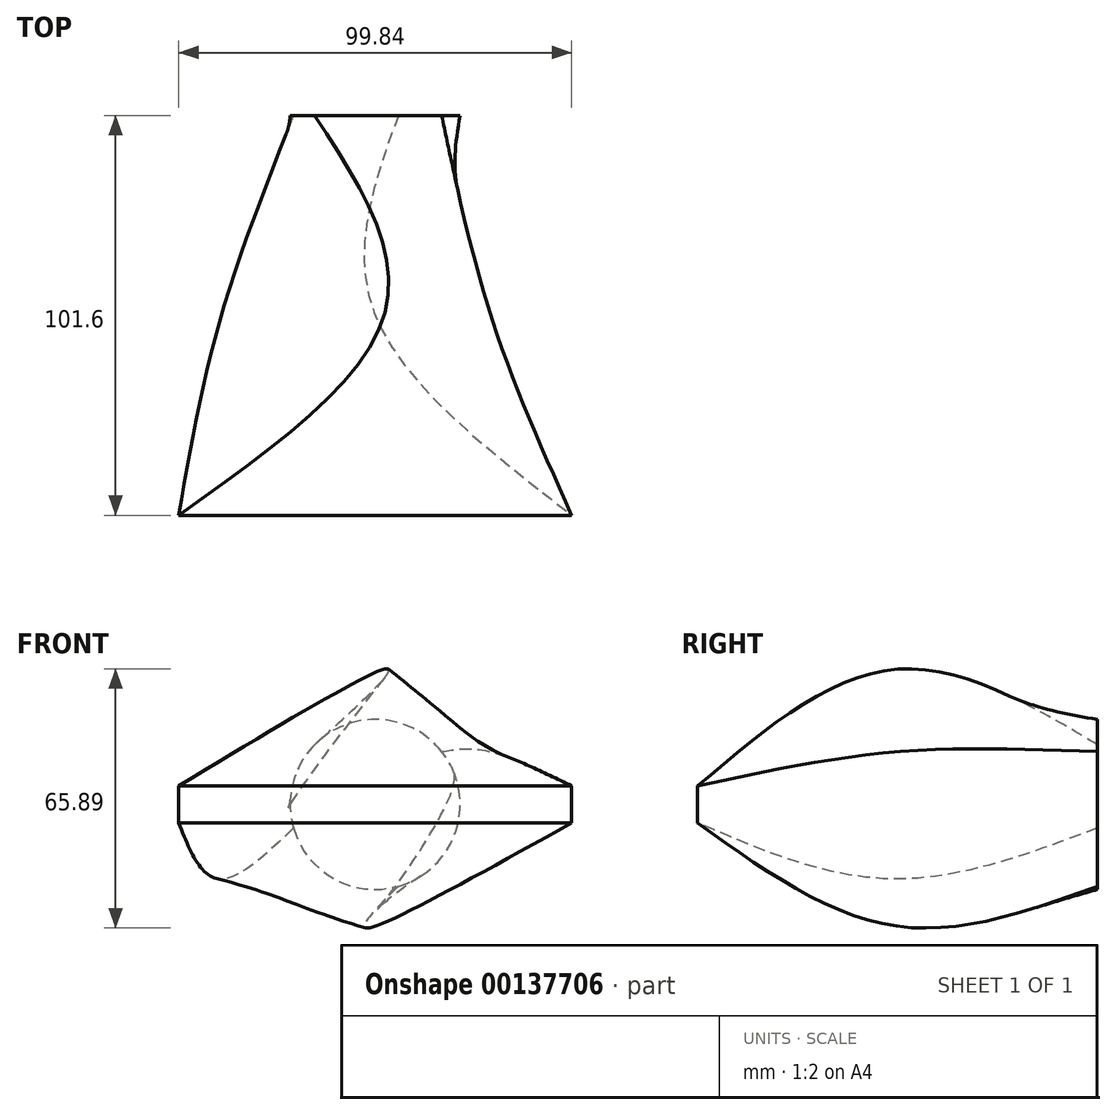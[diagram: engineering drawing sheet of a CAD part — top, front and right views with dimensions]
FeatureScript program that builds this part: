
annotation { "Feature Type Name" : "Feature", "Feature Type Description" : "" }
export const myFeature = defineFeature(function(context is Context, id is Id, definition is map)
    precondition{}
    {
        {
            var Q0;
            Q0=qCreatedBy(makeId("Front.planeOp"),FACE);
            var sketch = newSketch(context, id + "F0", { "sketchPlane" : qUnion([Q0])});
            skArc(sketch, "E0", {"start": v(-15.37, 15.16) * mm, "mid": v(-20.93, 5.3) * mm, "end": v(-20.74, -6) * mm});
            skArc(sketch, "E1", {"start": v(16.92, 13.42) * mm, "mid": v(1.16, 21.56) * mm, "end": v(-15.37, 15.16) * mm});
            skArc(sketch, "E2", {"start": v(5.88, -20.78) * mm, "mid": v(20.55, -6.63) * mm, "end": v(16.92, 13.42) * mm});
            skArc(sketch, "E3", {"start": v(-20.74, -6) * mm, "mid": v(-10.48, -18.88) * mm, "end": v(5.88, -20.78) * mm});
            skSolve(sketch);
        }
        {
            var Q0;
            Q0=qCreatedBy(makeId("Front.planeOp"),FACE);
            cPlane(context, id + "F1", {"entities" : qUnion([Q0]), "cplaneType" : CPlaneType.OFFSET, "offset" : 101.6 * mm, "width" : 152.4 * mm, "height" : 152.4 * mm});
        }
        {
            var Q0;
            Q0=qCreatedBy(id+"F1.planeOp",FACE);
            var sketch = newSketch(context, id + "F2", { "sketchPlane" : qUnion([Q0])});
            skLineSegment(sketch, "E4.bottom", {"start": v(-49.92, -4.7) * mm, "end": v(49.92, -4.7) * mm});
            skLineSegment(sketch, "E4.top", {"start": v(-49.92, 4.7) * mm, "end": v(49.92, 4.7) * mm});
            skLineSegment(sketch, "E4.left", {"start": v(-49.92, -4.7) * mm, "end": v(-49.92, 4.7) * mm});
            skLineSegment(sketch, "E4.right", {"start": v(49.92, -4.7) * mm, "end": v(49.92, 4.7) * mm});
            skPoint(sketch, "E4.middle", {"position": v(0, 0) * mm});
            skSolve(sketch);
        }
        {
            var Q0;
            Q0=qCreatedBy(makeId("Front.planeOp"),FACE);
            cPlane(context, id + "F3", {"entities" : qUnion([Q0]), "cplaneType" : CPlaneType.OFFSET, "offset" : 50.8 * mm, "width" : 152.4 * mm, "height" : 152.4 * mm});
        }
        {
            var Q0;
            Q0=qCreatedBy(id+"F3.planeOp",FACE);
            var sketch = newSketch(context, id + "F4", { "sketchPlane" : qUnion([Q0])});
            skLineSegment(sketch, "E5", {"start": v(-39.08, -18.97) * mm, "end": v(2.28, 34.37) * mm});
            skLineSegment(sketch, "E6", {"start": v(2.28, 34.37) * mm, "end": v(29.37, 13.37) * mm});
            skLineSegment(sketch, "E7", {"start": v(29.37, 13.37) * mm, "end": v(0, -30.95) * mm});
            skLineSegment(sketch, "E8", {"start": v(0, -30.95) * mm, "end": v(-39.08, -18.97) * mm});
            skSolve(sketch);
        }
        {
            var Q0;
            Q0 = qSketchRegion(id + "F0", true);
            var Q1;
            Q1 = qSketchRegion(id + "F4", true);
            var Q2;
            Q2 = qSketchRegion(id + "F2", true);
            loft(context, id + "F5", {"sheetProfilesArray" : [{ "sheetProfileEntities" : qUnion([Q0]) }, { "sheetProfileEntities" : qUnion([Q1]) }, { "sheetProfileEntities" : qUnion([Q2]) }]});
        }
    });
